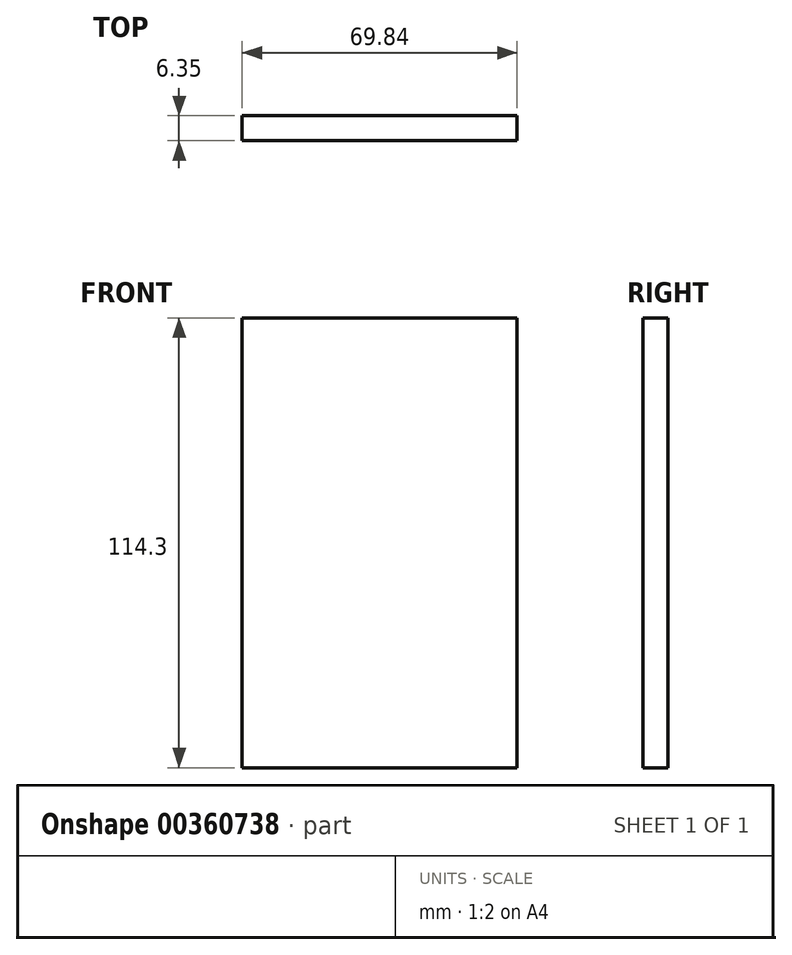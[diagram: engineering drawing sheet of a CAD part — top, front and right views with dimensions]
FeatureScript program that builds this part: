
annotation { "Feature Type Name" : "Feature", "Feature Type Description" : "" }
export const myFeature = defineFeature(function(context is Context, id is Id, definition is map)
    precondition{}
    {
        {
            var Q0;
            Q0=qCreatedBy(makeId("Front.planeOp"),FACE);
            var sketch = newSketch(context, id + "F0", { "sketchPlane" : qUnion([Q0])});
            skLineSegment(sketch, "E0.bottom", {"start": v(34.93, 57.15) * mm, "end": v(-34.92, 57.15) * mm});
            skLineSegment(sketch, "E0.top", {"start": v(34.92, -57.15) * mm, "end": v(-34.93, -57.15) * mm});
            skLineSegment(sketch, "E0.left", {"start": v(34.93, 57.15) * mm, "end": v(34.92, -57.15) * mm});
            skLineSegment(sketch, "E0.right", {"start": v(-34.93, 57.15) * mm, "end": v(-34.93, -57.15) * mm});
            skPoint(sketch, "E0.middle", {"position": v(0, 0) * mm});
            skSolve(sketch);
        }
        {
            var Q0;
            Q0=makeQuery(id+"F0.imprint","IMPRINT",FACE,{"disambiguationData":[TD([[makeQuery(id+"F0.imprint","IMPRINT",EDGE,{"derivedFrom":sQuery(id+"F0.wireOp",EDGE,"E0.bottom")}),1.0]])]});
            extrude(context, id + "F1", {"entities" : qUnion([Q0]), "depth" : 6.35 * mm});
        }
    });
